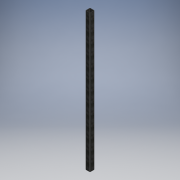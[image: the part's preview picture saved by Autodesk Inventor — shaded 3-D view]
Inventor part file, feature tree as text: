
AUTODESK INVENTOR PART (.ipt)
format: ipt  version: 2018 (Build 220112000, 112)  size: 111,104 bytes
history: native  units: mm
features: other x1, extrude x1, fillet x1, sketch x1
ambient origin geometry x8: Origin, YZ Plane, XZ Plane, XY Plane, X Axis, Y Axis, Z Axis, Center Point
bodies: Body1 (feature_tree)
feature tree (4):
  other  "Sólido1"
  extrude  "Extrusión1"  Depth=75.0mm
  fillet  "Empalme1"  Radius=3.0mm
  sketch  "Boceto1"  dims[d0=75.0mm d1=75.0mm d2=3.0mm d3=2350.0mm d4=0.0mm d5=6.0mm]
